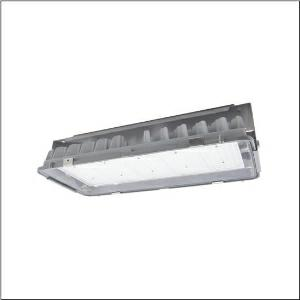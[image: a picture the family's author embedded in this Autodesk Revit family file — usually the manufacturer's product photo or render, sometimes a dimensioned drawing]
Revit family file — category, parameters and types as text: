
# Revit family: highbay_11xtreme_51hf61da4mma
name_source: partatom
category: Lighting Fixtures
units: mm (PartAtom-declared; Revit-internal decimal feet)

## family parameters
Cut with Voids When Loaded = No
Host = Face
Light Source = No
Part Type = Normal
Room Calculation Point = No
Round Connector Dimension = Use Diameter
Shared = No

## types (1)
- --- (1 x LED, 31500 lm, 170.8 W, 4000K)
    Apparent Load = 171 VA
    CIE Flux Codes = 88 96 99 100 100
    Color Rendering = 80
    Color Temperature = 4000K
    Default Elevation = 1800 mm
    Description = Highbay 11Xtreme, high bay luminaire, primary light control with lens, of PMMA, primary optical cover: cover, of toughened safety glass, light emission: direct distribution, primary light characteristic: symmetric, installation type: suspended mounting, surface-mounted, 1x LED module,for 1x LED, rated luminous flux: 31.500lm, luminous efficacy: 184lm/W, light colour: 840, colour temperature: 4000K, control gear: DALI 2, with cable H07RN-F 5x 1.5mm², mains connection: 220..240V, AC, 50/60Hz, cable length: 1,5m, rated input power: 171W, luminaire housing, of diecast aluminium, coated, silver, length: 595mm, width: 280mm, height: 195mm, protection rating (complete): IP66, insulation class (complete): insulation class I (protective earthing), certification: CE, ENEC, UKCA, protection symbol: D, ball protection: ball impact resistant according to DIN VDE 0710 part 13 (with chain suspension), impact resistance: IK08, permissible operating ambient temperature: -25..+60°C, reducing of maximum allowable ambient temperature of 5°C with ceiling mounting, packaging unit: 1 piece
    Height = 157 mm
    Lamp = 1 x LED
    Lamp Light Flux = 31500 lm
    Lamp Power = 170.8 W
    Lamp count = 1
    Length = 593 mm
    Luminous efficacy = 184 lm/W
    Manufacturer = Siteco
    ModVariant = No
    Model = 51HF61DA4MMA
    Mounting Place = Ceiling
    Mounting Type = Pendant
    Number of Poles = 1
    OnlyDefault = Yes
    Power Factor = 1
    Product Name = Highbay 11Xtreme
    Product group = high bay luminaire
    ProductGroupID = 901
    Protection Class = Protection class I
    Protection Degree = IP 66
    RLX_Detail_Level = 1
    RLX_Emergency_Light_Flux = 0 lm
    RLX_Emergency_Type = 0
    RLX_Emergency_Type_DB = No
    RlxData = <blob elided: 27905 chars, md5=4e734d31>
    Socket = socket
    Standby Power = 0 W
    System Light Flux = 31501 lm
    System Power = 171 W
    Type Comments = factory setting: luminous flux: 100 % | dim-lin: 254 | 1132 mA
    Type Image = l_1258342.jpg
    URL = http://relux.com
    VarID = @adj_083446
    Voltage = 0 V
    Weight = 0.00 kg
    Width = 278 mm

## geometry (parser evidence)
native form markers: Blend x4, Sweep x10
no freeform markers — native parametric forms only
